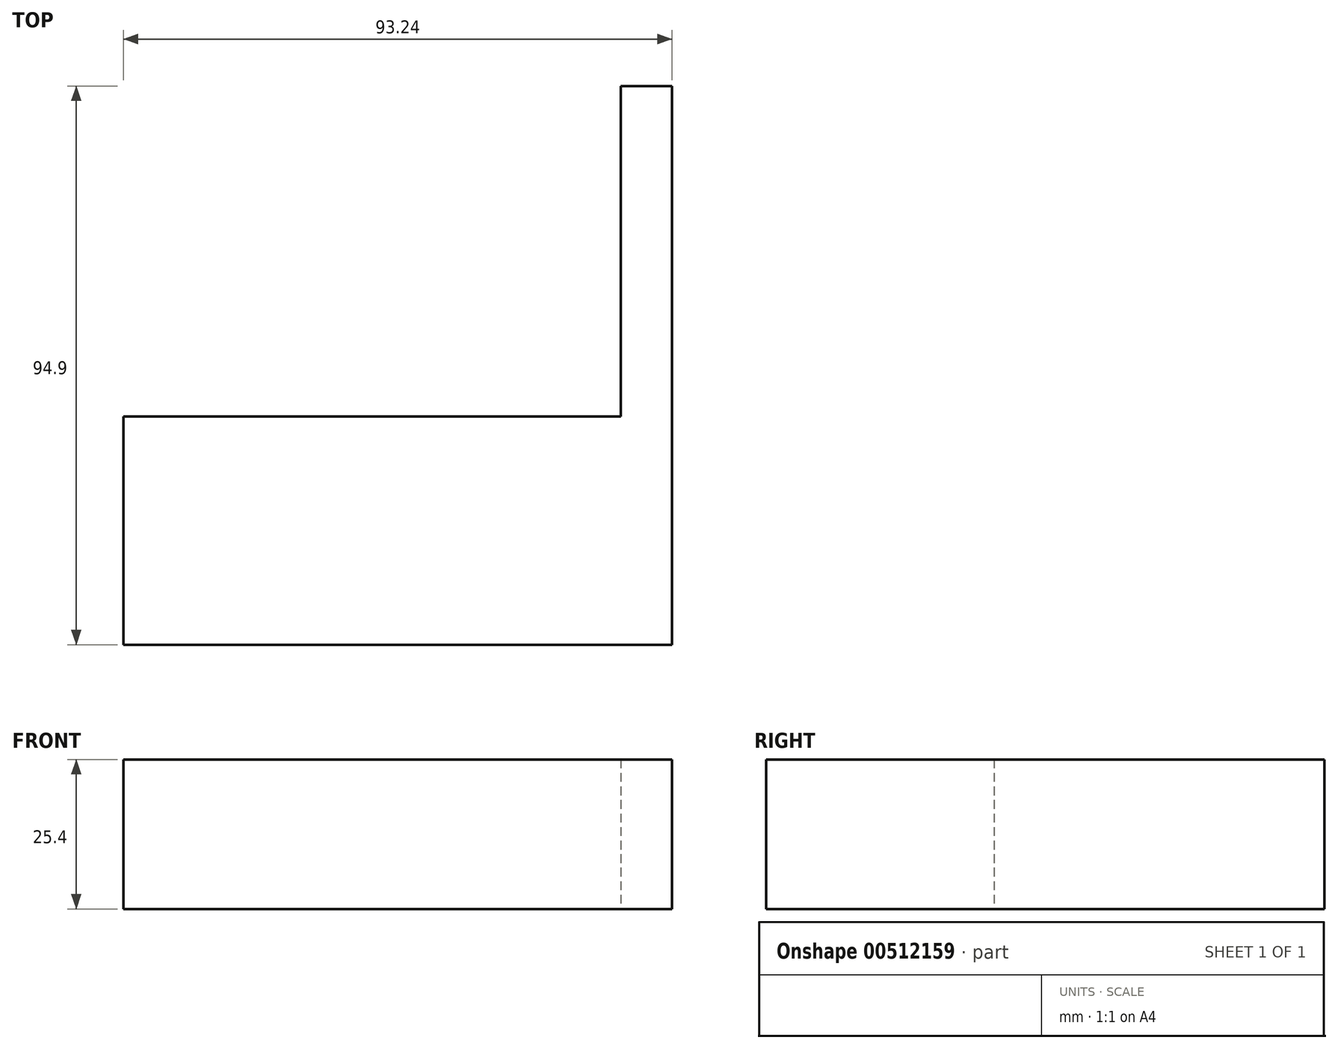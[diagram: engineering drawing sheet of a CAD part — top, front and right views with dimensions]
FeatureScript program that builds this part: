
annotation { "Feature Type Name" : "Feature", "Feature Type Description" : "" }
export const myFeature = defineFeature(function(context is Context, id is Id, definition is map)
    precondition{}
    {
        {
            var Q0;
            Q0=qCreatedBy(makeId("Top.planeOp"),FACE);
            var sketch = newSketch(context, id + "F0", { "sketchPlane" : qUnion([Q0])});
            skLineSegment(sketch, "E0.bottom", {"start": v(-93.24, 0) * mm, "end": v(-8.7, 0) * mm});
            skLineSegment(sketch, "E0.top", {"start": v(-93.24, -38.76) * mm, "end": v(-8.7, -38.76) * mm});
            skLineSegment(sketch, "E0.left", {"start": v(-93.24, 0) * mm, "end": v(-93.24, -38.76) * mm});
            skLineSegment(sketch, "E0.right", {"start": v(-8.7, 0) * mm, "end": v(-8.7, -38.76) * mm});
            skLineSegment(sketch, "E1.bottom", {"start": v(-8.7, -38.76) * mm, "end": v(0, -38.76) * mm});
            skLineSegment(sketch, "E1.top", {"start": v(-8.7, 56.14) * mm, "end": v(0, 56.14) * mm});
            skLineSegment(sketch, "E1.left", {"start": v(-8.7, -38.76) * mm, "end": v(-8.7, 56.14) * mm});
            skLineSegment(sketch, "E1.right", {"start": v(0, -38.76) * mm, "end": v(0, 56.14) * mm});
            skSolve(sketch);
        }
        {
            var Q0;
            Q0 = qSketchRegion(id + "F0", true);
            extrude(context, id + "F1", {"entities" : qUnion([Q0]), "depth" : 25.4 * mm});
        }
    });
